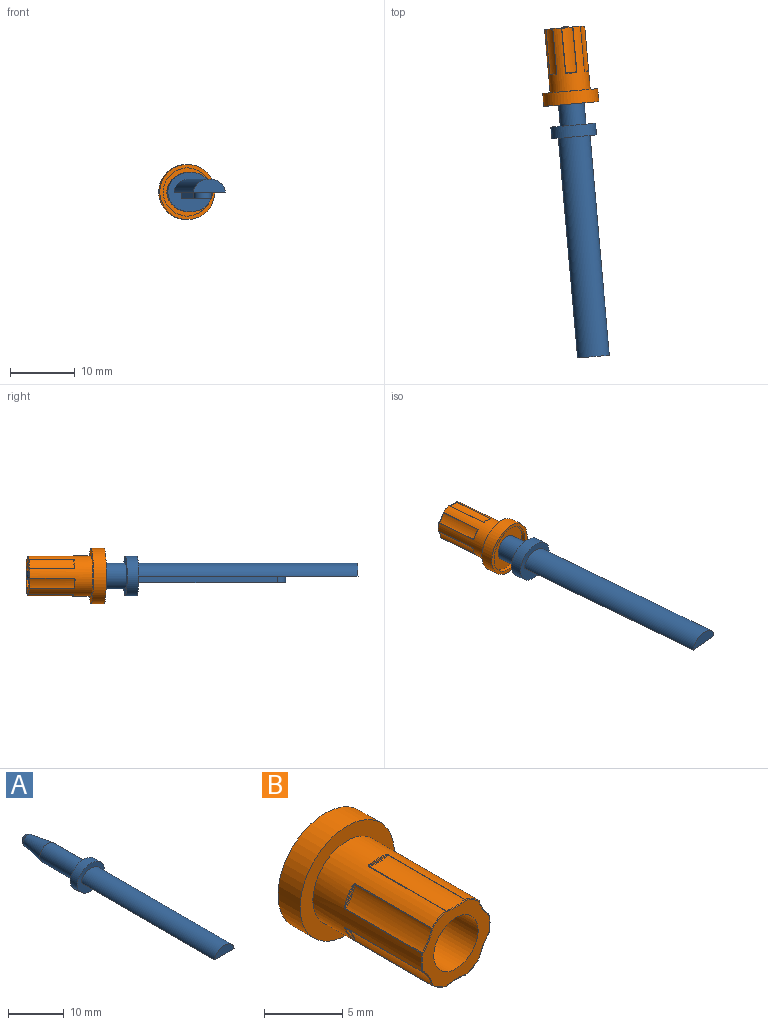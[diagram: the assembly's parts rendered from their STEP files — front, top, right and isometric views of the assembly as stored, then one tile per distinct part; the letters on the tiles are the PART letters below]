
ASSEMBLY  parts=2 mates=1
PART A: 14 faces, bbox 6.9x51x6.1 mm
  f0: plane 6.9x6.1mm, normal (0,-1,0), area 22.7mm2, adj f1,f2,f4,f10,f11,f13
  f1: plane 34x4.9mm, normal (0,0,-1), area 105.3mm2, adj f0,f2,f3,f10,f11,f12
  f2: extruded ~34x4.9mm, area 238.3mm2, adj f0,f1,f3
  f3: plane 4.9x2mm, normal (0,-1,0), area 7.7mm2, adj f1,f2
  f4: extruded ~6.9x6.1mm, area 36.8mm2, adj f0,f5
  f5: plane 6.9x6.1mm, normal (0,1,0), area 20.6mm2, adj f4,f6
  f6: cylinder r=1.99mm len=9.15mm, axis (0,-1,0), area 114.4mm2, adj f5,f8
  f7: plane 0.3x0.3mm, normal (0,1,0), area 0.1mm2, adj f9
  f8: bspline ~5.27x3.98mm, area 52.2mm2, adj f6,f9
  f9: bspline ~2.27x2.27mm, area 6.6mm2, adj f7,f8
  f10: plane 21.65x1mm, normal (-1,0,0), area 21.7mm2, adj f0,f1,f12,f13
  f11: plane 21.65x1mm, normal (1,0,0), area 21.7mm2, adj f0,f1,f12,f13
  f12: cylinder r=1.35mm len=2.7mm, axis (0,0,1), area 4.2mm2, adj f1,f10,f11,f13
  f13: plane 23x2.7mm, normal (0,0,-1), area 61.3mm2, adj f0,f10,f11,f12
PART B: 80 faces, bbox 8.5x11.8x8.5 mm
  f0: cylinder r=2mm len=11.2mm, axis (0,-1,0), area 140.7mm2, adj f5,f79
  f1: cylinder r=4.25mm len=8.5mm, axis (0,1,0), area 53.4mm2, adj f2,f3
  f2: plane 8.5x8.5mm, normal (0,-1,0), area 26.6mm2, adj f1,f4
  f3: plane 8.5x8.5mm, normal (0,1,0), area 13.5mm2, adj f1,f78
  f4: cylinder r=3.1mm len=9.75mm, axis (0,1,0), area 114.6mm2, adj f2,f8,f9,f11,f12,f13,f16,f17
  f5: plane 6.1x5.86mm, normal (0,-1,0), area 14.9mm2, adj f0,f54,f57,f58,f61,f62,f65,f66
  f6: extruded ~6.9x1.7mm, area 11.9mm2, adj f8,f10,f13,f66
  f7: plane 1.38x0.15mm, normal (0,-1,0), area 0.1mm2, adj f10,f11
  f8: cylinder r=0.05mm len=6.9mm, axis (0,-1,0), area 0.2mm2, adj f4,f6,f9,f64
  f9: bspline ~0.21x0.12mm, area 0mm2, adj f4,f8,f10,f11
  f10: bspline ~1.83x0.2mm, area 0.1mm2, adj f6,f7,f9,f12
  f11: torus R=3.05mm, axis (0,-1,0), area 0.1mm2, adj f4,f7,f9,f12
  f12: bspline ~0.31x0.11mm, area 0mm2, adj f4,f10,f11,f13
  f13: cylinder r=0.05mm len=6.9mm, axis (0,-1,0), area 0.2mm2, adj f4,f6,f12,f68
  f14: extruded ~6.9x1.48mm, area 11.9mm2, adj f16,f18,f21,f58
  f15: plane 1.2x0.68mm, normal (0,-1,0), area 0.1mm2, adj f18,f19
  f16: cylinder r=0.05mm len=6.9mm, axis (0,-1,0), area 0.2mm2, adj f4,f14,f17,f56
  f17: bspline ~0.2x0.12mm, area 0mm2, adj f4,f16,f18,f19
  f18: bspline ~1.49x0.87mm, area 0.1mm2, adj f14,f15,f17,f20
  f19: torus R=3.05mm, axis (0,-1,0), area 0.1mm2, adj f4,f15,f17,f20
  f20: bspline ~0.27x0.21mm, area 0mm2, adj f4,f18,f19,f21
  f21: cylinder r=0.05mm len=6.9mm, axis (0,-1,0), area 0.2mm2, adj f4,f14,f20,f60
  f22: extruded ~6.9x1.47mm, area 11.9mm2, adj f24,f26,f29,f57
  f23: plane 1.19x0.7mm, normal (0,-1,0), area 0.1mm2, adj f26,f27
  f24: cylinder r=0.05mm len=6.9mm, axis (0,-1,0), area 0.2mm2, adj f4,f22,f25,f59
  f25: bspline ~0.18x0.15mm, area 0mm2, adj f4,f24,f26,f27
  f26: bspline ~1.57x0.95mm, area 0.1mm2, adj f22,f23,f25,f28
  f27: torus R=3.05mm, axis (0,-1,0), area 0.1mm2, adj f4,f23,f25,f28
  f28: bspline ~0.3x0.16mm, area 0mm2, adj f4,f26,f27,f29
  f29: cylinder r=0.05mm len=6.9mm, axis (0,-1,0), area 0.2mm2, adj f4,f22,f28,f55
  f30: extruded ~6.9x1.7mm, area 11.9mm2, adj f32,f34,f37,f65
  f31: plane 1.38x0.15mm, normal (0,-1,0), area 0.1mm2, adj f34,f35
  f32: cylinder r=0.05mm len=6.9mm, axis (0,-1,0), area 0.2mm2, adj f4,f30,f33,f67
  f33: bspline ~0.21x0.12mm, area 0mm2, adj f4,f32,f34,f35
  f34: bspline ~1.83x0.2mm, area 0.1mm2, adj f30,f31,f33,f36
  f35: torus R=3.05mm, axis (0,-1,0), area 0.1mm2, adj f4,f31,f33,f36
  f36: bspline ~0.31x0.11mm, area 0mm2, adj f4,f34,f35,f37
  f37: cylinder r=0.05mm len=6.9mm, axis (0,-1,0), area 0.2mm2, adj f4,f30,f36,f63
  f38: extruded ~6.9x1.48mm, area 11.9mm2, adj f40,f42,f45,f73
  f39: plane 1.2x0.68mm, normal (0,-1,0), area 0.1mm2, adj f42,f43
  f40: cylinder r=0.05mm len=6.9mm, axis (0,-1,0), area 0.2mm2, adj f4,f38,f41,f75
  f41: bspline ~0.2x0.12mm, area 0mm2, adj f4,f40,f42,f43
  f42: bspline ~1.49x0.87mm, area 0.1mm2, adj f38,f39,f41,f44
  f43: torus R=3.05mm, axis (0,-1,0), area 0.1mm2, adj f4,f39,f41,f44
  f44: bspline ~0.27x0.21mm, area 0mm2, adj f4,f42,f43,f45
  f45: cylinder r=0.05mm len=6.9mm, axis (0,-1,0), area 0.2mm2, adj f4,f38,f44,f71
  f46: extruded ~6.9x1.47mm, area 11.9mm2, adj f48,f50,f53,f74
  f47: plane 1.19x0.7mm, normal (0,-1,0), area 0.1mm2, adj f50,f51
  f48: cylinder r=0.05mm len=6.9mm, axis (0,-1,0), area 0.2mm2, adj f4,f46,f49,f72
  f49: bspline ~0.18x0.15mm, area 0mm2, adj f4,f48,f50,f51
  f50: bspline ~1.57x0.95mm, area 0.1mm2, adj f46,f47,f49,f52
  f51: torus R=3.05mm, axis (0,-1,0), area 0.1mm2, adj f4,f47,f49,f52
  f52: bspline ~0.3x0.16mm, area 0mm2, adj f4,f50,f51,f53
  f53: cylinder r=0.05mm len=6.9mm, axis (0,-1,0), area 0.2mm2, adj f4,f46,f52,f76
  f54: torus R=3.05mm, axis (0,-1,0), area 0.1mm2, adj f4,f5,f55,f56
  f55: sphere r=0.05mm, area 0mm2, adj f29,f54,f57
  f56: sphere r=0.05mm, area 0mm2, adj f16,f54,f58
  f57: bspline ~1.62x0.97mm, area 0.1mm2, adj f5,f22,f55,f59
  f58: bspline ~1.63x0.96mm, area 0.1mm2, adj f5,f14,f56,f60
  f59: sphere r=0.05mm, area 0mm2, adj f24,f57,f61
  f60: sphere r=0.05mm, area 0mm2, adj f21,f58,f62
  f61: torus R=3.05mm, axis (0,-1,0), area 0.1mm2, adj f4,f5,f59,f63
  f62: torus R=3.05mm, axis (0,-1,0), area 0.1mm2, adj f4,f5,f60,f64
  f63: sphere r=0.05mm, area 0mm2, adj f37,f61,f65
  f64: sphere r=0.05mm, area 0mm2, adj f8,f62,f66
  f65: bspline ~1.87x0.2mm, area 0.1mm2, adj f5,f30,f63,f67
  f66: bspline ~1.87x0.2mm, area 0.1mm2, adj f5,f6,f64,f68
  f67: sphere r=0.05mm, area 0mm2, adj f32,f65,f69
  f68: sphere r=0.05mm, area 0mm2, adj f13,f66,f70
  f69: torus R=3.05mm, axis (0,-1,0), area 0.1mm2, adj f4,f5,f67,f71
  f70: torus R=3.05mm, axis (0,-1,0), area 0.1mm2, adj f4,f5,f68,f72
  f71: sphere r=0.05mm, area 0mm2, adj f45,f69,f73
  f72: sphere r=0.05mm, area 0mm2, adj f48,f70,f74
  f73: bspline ~1.63x0.96mm, area 0.1mm2, adj f5,f38,f71,f75
  f74: bspline ~1.62x0.97mm, area 0.1mm2, adj f5,f46,f72,f76
  f75: sphere r=0.05mm, area 0mm2, adj f40,f73,f77
  f76: sphere r=0.05mm, area 0mm2, adj f53,f74,f77
  f77: torus R=3.05mm, axis (0,-1,0), area 0.1mm2, adj f4,f5,f75,f76
  f78: cylinder r=3.71mm len=7.42mm, axis (0,1,0), area 14mm2, adj f3,f79
  f79: plane 7.42x7.42mm, normal (0,1,0), area 30.7mm2, adj f0,f78
PLACE A rot(axis=(0,0,1),5deg) t=(21.41,-21.51,6.88)mm fixed
PLACE B rot(axis=(-0.55,-0.02,-0.83),175.8deg) t=(18,17.43,6.88)mm
MATE cylindrical A.f6 <-> B.f0  axis (0.09,-1,0) through (17.89,18.72,6.88)mm
